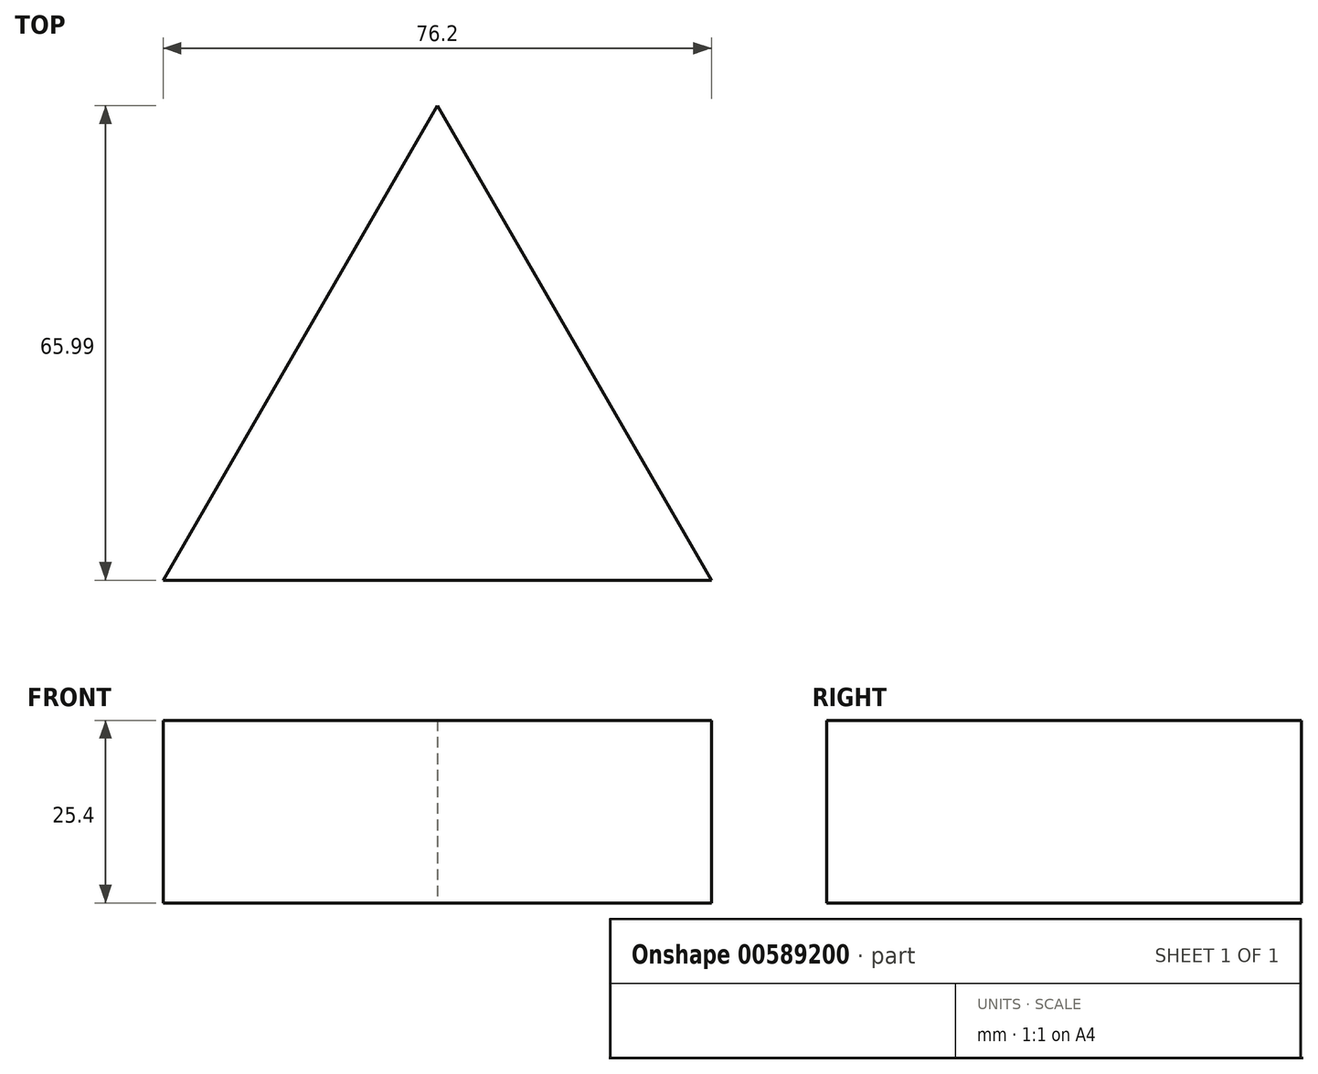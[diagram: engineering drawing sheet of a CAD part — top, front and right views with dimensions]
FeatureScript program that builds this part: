
annotation { "Feature Type Name" : "Feature", "Feature Type Description" : "" }
export const myFeature = defineFeature(function(context is Context, id is Id, definition is map)
    precondition{}
    {
        {
            var Q0;
            Q0=qCreatedBy(makeId("Top.planeOp"),FACE);
            var sketch = newSketch(context, id + "F0", { "sketchPlane" : qUnion([Q0])});
            skLineSegment(sketch, "E0", {"start": v(0, 38.67) * mm, "end": v(-38.1, -27.32) * mm});
            skLineSegment(sketch, "E1", {"start": v(-38.1, -27.32) * mm, "end": v(38.1, -27.32) * mm});
            skLineSegment(sketch, "E2", {"start": v(38.1, -27.32) * mm, "end": v(0, 38.67) * mm});
            skSolve(sketch);
        }
        {
            var Q0;
            Q0 = qSketchRegion(id + "F0", true);
            extrude(context, id + "F1", {"entities" : qUnion([Q0]), "depth" : 25.4 * mm, "offsetDistance" : 25.4 * mm});
        }
    });
